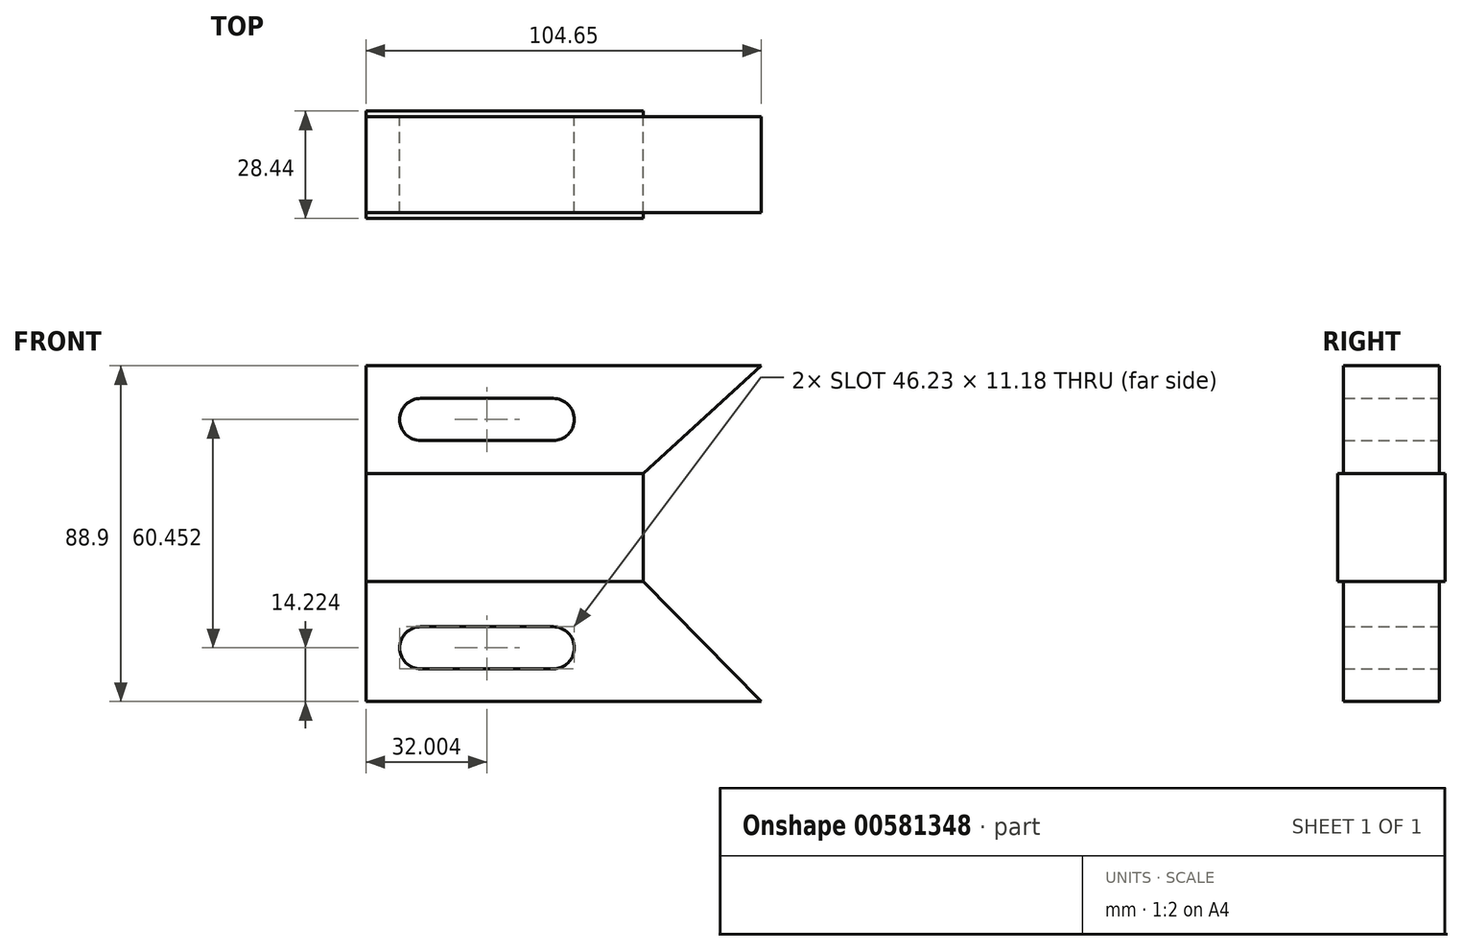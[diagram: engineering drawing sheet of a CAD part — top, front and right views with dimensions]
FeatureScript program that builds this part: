
annotation { "Feature Type Name" : "Feature", "Feature Type Description" : "" }
export const myFeature = defineFeature(function(context is Context, id is Id, definition is map)
    precondition{}
    {
        {
            var Q0;
            Q0=qCreatedBy(makeId("Front.planeOp"),FACE);
            var sketch = newSketch(context, id + "F0", { "sketchPlane" : qUnion([Q0])});
            skLineSegment(sketch, "E0", {"start": v(0, 0) * mm, "end": v(0, 88.9) * mm});
            skLineSegment(sketch, "E1", {"start": v(0, 88.9) * mm, "end": v(104.65, 88.9) * mm});
            skLineSegment(sketch, "E2", {"start": v(14.48, 74.68) * mm, "end": v(49.53, 74.68) * mm});
            skArc(sketch, "E3.0.startCap", {"start": v(14.48, 69.09) * mm, "mid": v(8.89, 74.68) * mm, "end": v(14.48, 80.26) * mm});
            skArc(sketch, "E3.0.endCap", {"start": v(49.53, 80.26) * mm, "mid": v(55.12, 74.68) * mm, "end": v(49.53, 69.09) * mm});
            skLineSegment(sketch, "E3.0.left", {"start": v(14.48, 80.26) * mm, "end": v(49.53, 80.26) * mm});
            skLineSegment(sketch, "E3.0.right", {"start": v(14.48, 69.09) * mm, "end": v(49.53, 69.09) * mm});
            skLineSegment(sketch, "E4", {"start": v(73.4, 60.33) * mm, "end": v(0, 60.33) * mm});
            skLineSegment(sketch, "E5", {"start": v(73.4, 60.33) * mm, "end": v(73.4, 88.9) * mm, "construction": true});
            skLineSegment(sketch, "E6", {"start": v(104.65, 88.9) * mm, "end": v(73.4, 60.33) * mm});
            skLineSegment(sketch, "E7", {"start": v(73.4, 60.33) * mm, "end": v(73.4, 31.75) * mm});
            skLineSegment(sketch, "E8", {"start": v(73.4, 31.75) * mm, "end": v(0, 31.75) * mm});
            skLineSegment(sketch, "E9", {"start": v(0, 0) * mm, "end": v(104.65, 0) * mm});
            skLineSegment(sketch, "E10", {"start": v(104.65, 0) * mm, "end": v(73.4, 31.75) * mm});
            skLineSegment(sketch, "E11", {"start": v(14.48, 14.22) * mm, "end": v(49.53, 14.22) * mm});
            skArc(sketch, "E12.0.startCap", {"start": v(14.48, 8.64) * mm, "mid": v(8.89, 14.22) * mm, "end": v(14.48, 19.81) * mm});
            skArc(sketch, "E12.0.endCap", {"start": v(49.53, 19.81) * mm, "mid": v(55.12, 14.22) * mm, "end": v(49.53, 8.64) * mm});
            skLineSegment(sketch, "E12.0.left", {"start": v(14.48, 19.81) * mm, "end": v(49.53, 19.81) * mm});
            skLineSegment(sketch, "E12.0.right", {"start": v(14.48, 8.64) * mm, "end": v(49.53, 8.64) * mm});
            skSolve(sketch);
        }
        {
            var Q0;
            Q0 = qSketchRegion(id + "F0", true);
            extrude(context, id + "F1", {"entities" : qUnion([Q0]), "depth" : 25.4 * mm, "offsetDistance" : 25.4 * mm});
        }
        {
            var Q0;
            Q0=makeQuery(id+"F1.opExtrude","CAP_FACE",FACE,{"disambiguationData":[OSD([sQuery(id+"F0.wireOp",EDGE,"E0"),sQuery(id+"F0.wireOp",EDGE,"E1"),sQuery(id+"F0.wireOp",EDGE,"E3.0.startCap"),sQuery(id+"F0.wireOp",EDGE,"E3.0.endCap"),sQuery(id+"F0.wireOp",EDGE,"E3.0.left"),sQuery(id+"F0.wireOp",EDGE,"E3.0.right"),sQuery(id+"F0.wireOp",EDGE,"E6"),sQuery(id+"F0.wireOp",EDGE,"E7"),sQuery(id+"F0.wireOp",EDGE,"E9"),sQuery(id+"F0.wireOp",EDGE,"E10"),sQuery(id+"F0.wireOp",EDGE,"E12.0.startCap"),sQuery(id+"F0.wireOp",EDGE,"E12.0.endCap"),sQuery(id+"F0.wireOp",EDGE,"E12.0.left"),sQuery(id+"F0.wireOp",EDGE,"E12.0.right")])],"isStart":false});
            var sketch = newSketch(context, id + "F2", { "sketchPlane" : qUnion([Q0])});
            skLineSegment(sketch, "E13", {"start": v(73.4, 60.33) * mm, "end": v(0, 60.33) * mm});
            skLineSegment(sketch, "E14", {"start": v(0, 60.33) * mm, "end": v(0, 31.75) * mm});
            skLineSegment(sketch, "E15", {"start": v(0, 31.75) * mm, "end": v(73.4, 31.75) * mm});
            skLineSegment(sketch, "E16", {"start": v(73.4, 31.75) * mm, "end": v(73.4, 60.33) * mm});
            skSolve(sketch);
        }
        {
            var Q0;
            Q0 = qSketchRegion(id + "F2", true);
            extrude(context, id + "F3", {"entities" : qUnion([Q0]), "operationType" : NewBodyOperationType.ADD, "depth" : 1.52 * mm, "offsetDistance" : 25.4 * mm});
        }
        {
            var Q0;
            Q0=makeQuery(id+"F1.opExtrude","CAP_FACE",FACE,{"disambiguationData":[OSD([sQuery(id+"F0.wireOp",EDGE,"E0"),sQuery(id+"F0.wireOp",EDGE,"E1"),sQuery(id+"F0.wireOp",EDGE,"E3.0.startCap"),sQuery(id+"F0.wireOp",EDGE,"E3.0.endCap"),sQuery(id+"F0.wireOp",EDGE,"E3.0.left"),sQuery(id+"F0.wireOp",EDGE,"E3.0.right"),sQuery(id+"F0.wireOp",EDGE,"E6"),sQuery(id+"F0.wireOp",EDGE,"E7"),sQuery(id+"F0.wireOp",EDGE,"E9"),sQuery(id+"F0.wireOp",EDGE,"E10"),sQuery(id+"F0.wireOp",EDGE,"E12.0.startCap"),sQuery(id+"F0.wireOp",EDGE,"E12.0.endCap"),sQuery(id+"F0.wireOp",EDGE,"E12.0.left"),sQuery(id+"F0.wireOp",EDGE,"E12.0.right")])],"isStart":true});
            var sketch = newSketch(context, id + "F4", { "sketchPlane" : qUnion([Q0])});
            skLineSegment(sketch, "E17", {"start": v(-73.4, 60.33) * mm, "end": v(0, 60.33) * mm});
            skLineSegment(sketch, "E18", {"start": v(0, 60.33) * mm, "end": v(0, 31.75) * mm});
            skLineSegment(sketch, "E19", {"start": v(0, 31.75) * mm, "end": v(-73.4, 31.75) * mm});
            skLineSegment(sketch, "E20", {"start": v(-73.4, 31.75) * mm, "end": v(-73.4, 60.33) * mm});
            skSolve(sketch);
        }
        {
            var Q0;
            Q0 = qSketchRegion(id + "F4", true);
            extrude(context, id + "F5", {"entities" : qUnion([Q0]), "operationType" : NewBodyOperationType.ADD, "depth" : 1.52 * mm, "offsetDistance" : 25.4 * mm});
        }
    });
